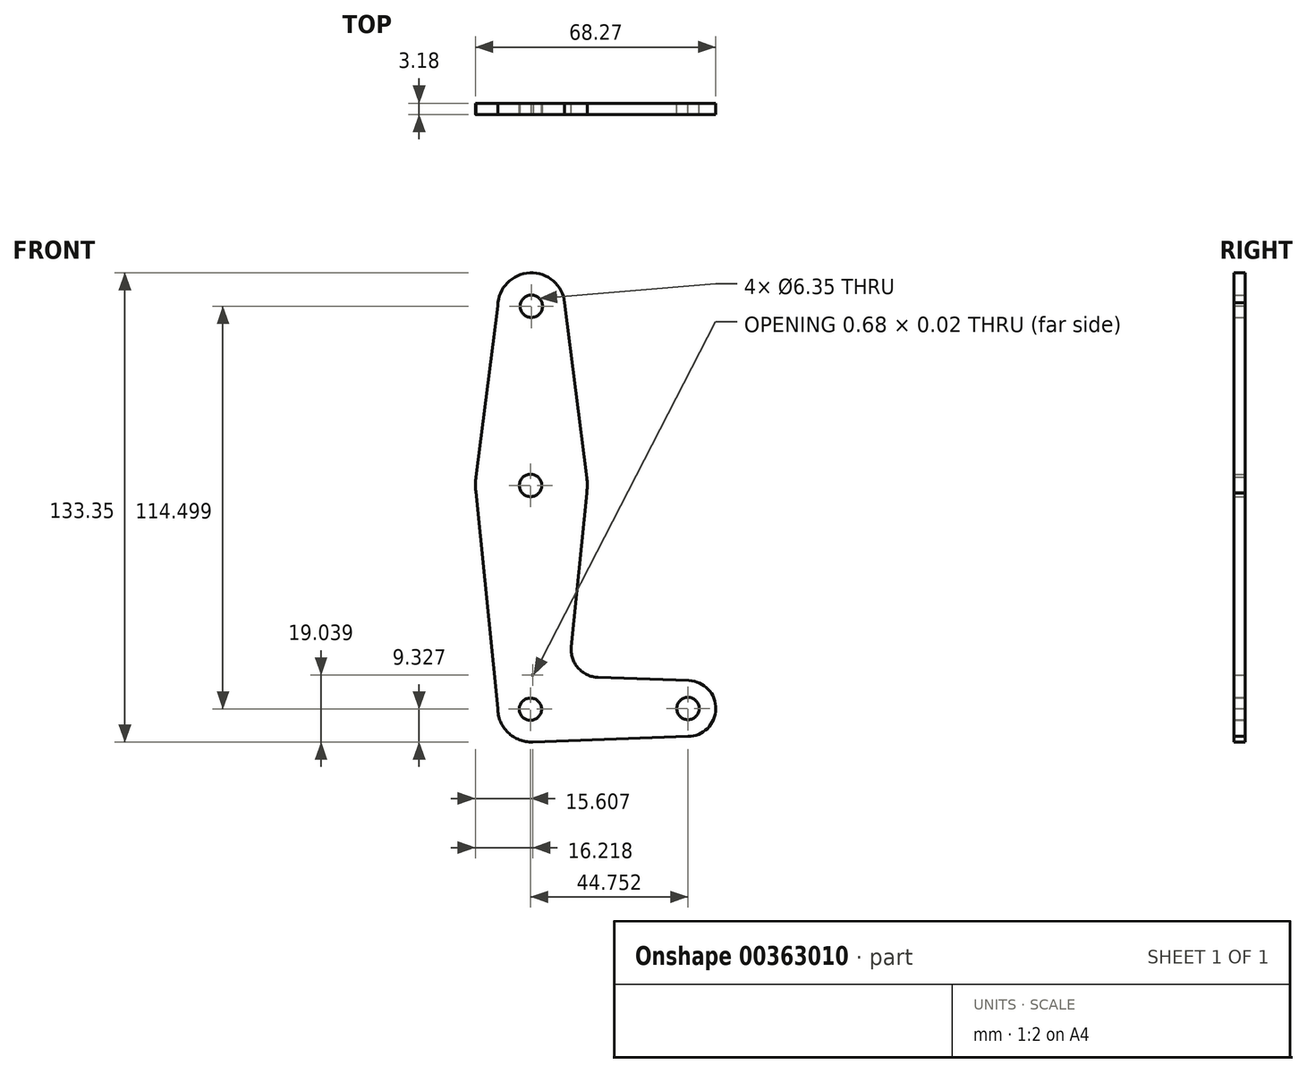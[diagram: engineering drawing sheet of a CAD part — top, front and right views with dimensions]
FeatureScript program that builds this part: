
annotation { "Feature Type Name" : "Feature", "Feature Type Description" : "" }
export const myFeature = defineFeature(function(context is Context, id is Id, definition is map)
    precondition{}
    {
        {
            var Q0;
            Q0=qCreatedBy(makeId("Front.planeOp"),FACE);
            var sketch = newSketch(context, id + "F0", { "sketchPlane" : qUnion([Q0])});
            skLineSegment(sketch, "E0", {"start": v(-128.46, 109.02) * mm, "end": v(-128.46, 58.22) * mm, "construction": true});
            skLineSegment(sketch, "E1", {"start": v(-128.46, 58.22) * mm, "end": v(-128.46, -5.28) * mm, "construction": true});
            skLineSegment(sketch, "E2", {"start": v(-128.46, -5.28) * mm, "end": v(-84.01, -5.28) * mm, "construction": true});
            skCircle(sketch, "E3", {"center": v(-128.46, 109.02) * mm, "radius": 9.53 * mm});
            skCircle(sketch, "E4", {"center": v(-128.46, 58.22) * mm, "radius": 15.88 * mm});
            skCircle(sketch, "E5", {"center": v(-128.46, -5.28) * mm, "radius": 9.53 * mm});
            skCircle(sketch, "E6", {"center": v(-84.01, -5.28) * mm, "radius": 7.94 * mm});
            skLineSegment(sketch, "E7", {"start": v(-118.99, 110.02) * mm, "end": v(-112.7, 60.2) * mm});
            skLineSegment(sketch, "E8", {"start": v(-118.9, -5.28) * mm, "end": v(-132.22, -4.03) * mm});
            skLineSegment(sketch, "E9", {"start": v(-128.46, 4.24) * mm, "end": v(-127.78, 4.22) * mm});
            skLineSegment(sketch, "E10", {"start": v(-84.02, -13.22) * mm, "end": v(-128.12, -14.8) * mm});
            skLineSegment(sketch, "E11", {"start": v(-137.99, -5.25) * mm, "end": v(-144.28, 56.9) * mm});
            skLineSegment(sketch, "E12", {"start": v(-144.24, 59.93) * mm, "end": v(-137.98, 109.18) * mm});
            skLineSegment(sketch, "E13", {"start": v(-112.6, 57.37) * mm, "end": v(-117.13, 12.28) * mm});
            skCircle(sketch, "E14", {"center": v(-128.46, 109.02) * mm, "radius": 3.18 * mm});
            skCircle(sketch, "E15", {"center": v(-128.68, 58.1) * mm, "radius": 3.18 * mm});
            skCircle(sketch, "E16", {"center": v(-128.73, -5.48) * mm, "radius": 3.18 * mm});
            skCircle(sketch, "E17", {"center": v(-83.98, -5.29) * mm, "radius": 3.18 * mm});
            skLineSegment(sketch, "E18.trimOffspring", {"start": v(-109.53, 3.57) * mm, "end": v(-83.73, 2.65) * mm});
            skPoint(sketch, "E19.visualSharp", {"position": v(-117.98, 3.87) * mm});
            skArc(sketch, "E19.filletArc", {"start": v(-117.13, 12.28) * mm, "mid": v(-115.22, 6.28) * mm, "end": v(-109.53, 3.57) * mm});
            skSolve(sketch);
        }
        {
            var Q0;
            Q0 = qSketchRegion(id + "F0", true);
            extrude(context, id + "F1", {"entities" : qUnion([Q0]), "depth" : 3.17 * mm});
        }
    });
